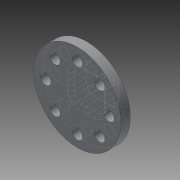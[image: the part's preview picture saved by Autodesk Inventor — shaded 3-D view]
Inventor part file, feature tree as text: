
AUTODESK INVENTOR PART (.ipt)
format: ipt  version: 2013 (Build 170138000, 138)  size: 154,112 bytes
history: native  units: mm
features: sketch x4, extrude x2, hole x2, fillet x1
ambient origin geometry x8: Origin, YZ Plane, XZ Plane, XY Plane, X Axis, Y Axis, Z Axis, Center Point
bodies: Solid1 (feature_tree)
feature tree (9):
  extrude  "Extrusion1"  Depth=6.0mm TaperAngle=0.0deg
  hole  "Hole1"  [1 undecoded]
  extrude  "Extrusion2"  Depth=5.0mm
  hole  "Hole2"  [1 undecoded]
  fillet  "Fillet1"  Radius=10.0mm
  sketch  "Sketch1"  dims[d0=55.0mm d1=6.0mm d2=0.0mm]
  sketch  "Sketch2"  dims[d3=20.0mm d4=80.0mm d6=360.0deg]
  sketch  "Sketch3"  dims[d8=6.6mm d9=6.0mm d10=12.6mm d11=2.0mm d12=90.0deg d13=8.0mm d14=20.594885mm d15=5.0mm]
  sketch  "Sketch4"  dims[d16=20.0mm d17=20.0mm d18=10.0mm d19=0.0mm d20=3.242mm d21=10.0mm d22=12.6mm d23=2.0mm d24=90.0deg d25=15.0mm d26=20.594885mm d27=2.0mm]
note: 2 required parameter values undecoded (feature->parameter linkage not recoverable at this tier; creation-order binding heuristic only, values carry confidence <= 0.55)
